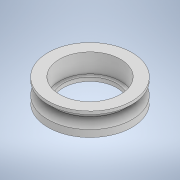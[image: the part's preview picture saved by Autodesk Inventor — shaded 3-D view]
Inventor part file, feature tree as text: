
AUTODESK INVENTOR PART (.ipt)
format: ipt  version: 2022.2 (Build 262287000, 287)  size: 131,584 bytes
history: native  units: mm
features: revolve x1, sketch x1
ambient origin geometry x8: Origin, YZ Plane, XZ Plane, XY Plane, X Axis, Y Axis, Z Axis, Center Point
bodies: Solid1 (feature_tree)
feature tree (2):
  revolve  "Revolution1"  [1 undecoded]
  sketch  "Sketch2"  dims[d1=1.0mm d2=1.0mm d3=5.0mm d4=1.0mm d5=8.0mm d8=90.0deg d9=2.0mm d10=3.0mm]
note: 1 required parameter value undecoded (feature->parameter linkage not recoverable at this tier; creation-order binding heuristic only, values carry confidence <= 0.55)
